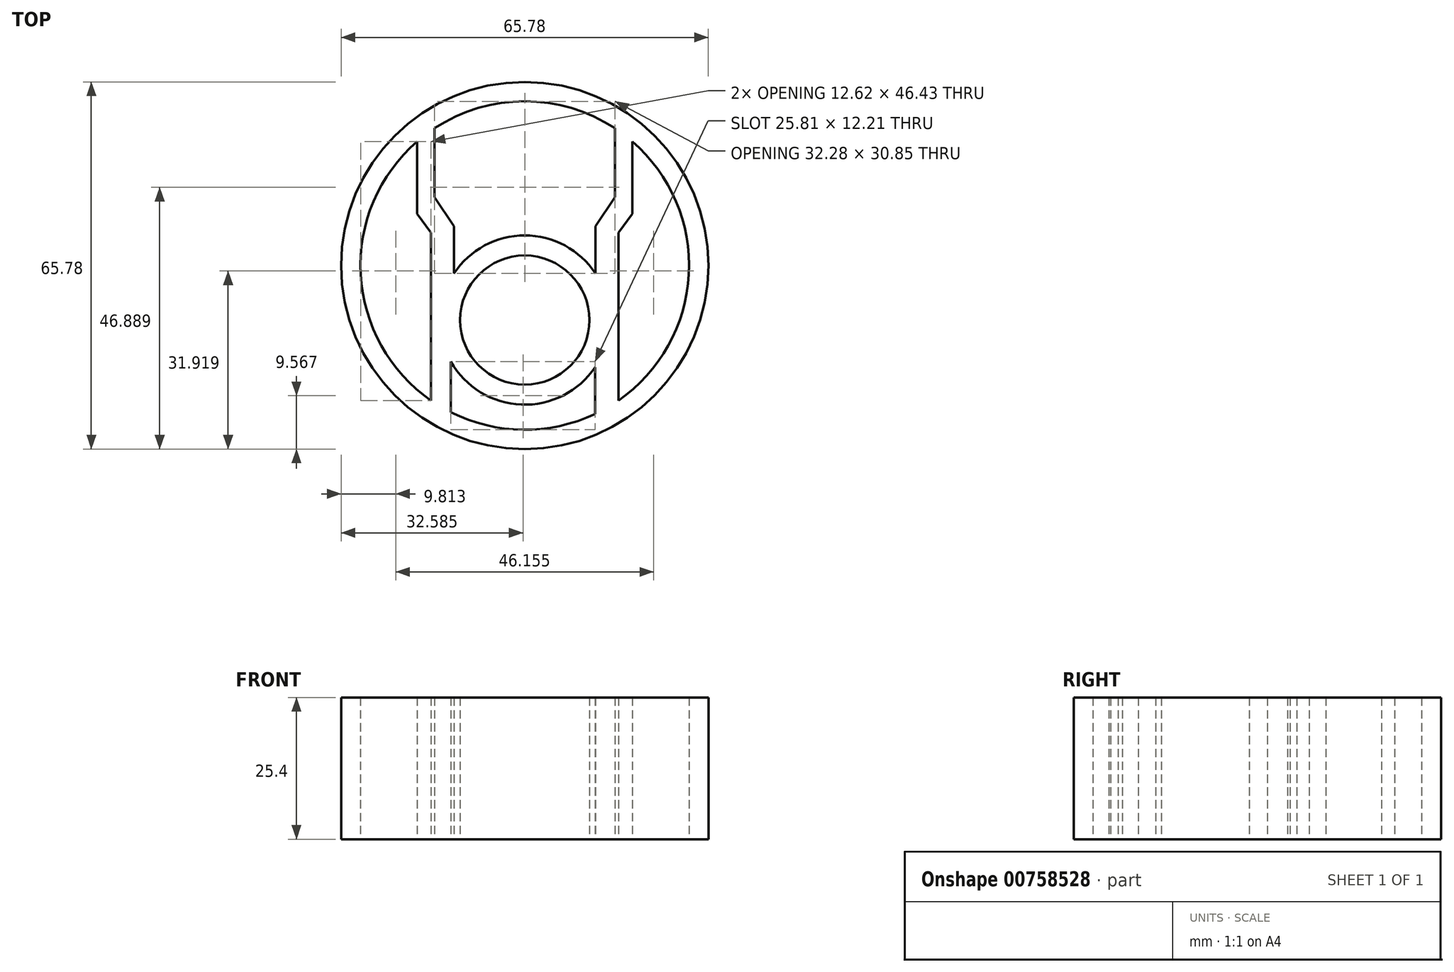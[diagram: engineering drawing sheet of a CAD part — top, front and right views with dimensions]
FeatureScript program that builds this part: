
annotation { "Feature Type Name" : "Feature", "Feature Type Description" : "" }
export const myFeature = defineFeature(function(context is Context, id is Id, definition is map)
    precondition{}
    {
        {
            var Q0;
            Q0=qCreatedBy(makeId("Top.planeOp"),FACE);
            var sketch = newSketch(context, id + "F0", { "sketchPlane" : qUnion([Q0])});
            skCircle(sketch, "E0", {"center": v(36.28, 37) * mm, "radius": 32.9 * mm});
            skArc(sketch, "E1", {"start": v(23.07, 10.7) * mm, "mid": v(35.94, 7.57) * mm, "end": v(48.88, 10.4) * mm});
            skCircle(sketch, "E2", {"center": v(36.28, 27.23) * mm, "radius": 11.58 * mm});
            skArc(sketch, "E3", {"start": v(23.07, 19.78) * mm, "mid": v(35.7, 12.07) * mm, "end": v(48.88, 18.79) * mm});
            skLineSegment(sketch, "E4", {"start": v(48.88, 10.4) * mm, "end": v(48.88, 18.79) * mm});
            skLineSegment(sketch, "E5", {"start": v(23.07, 10.7) * mm, "end": v(23.07, 19.78) * mm});
            skLineSegment(sketch, "E6", {"start": v(19.51, 12.81) * mm, "end": v(19.51, 42.89) * mm});
            skLineSegment(sketch, "E7", {"start": v(19.51, 42.89) * mm, "end": v(17.02, 46.27) * mm});
            skLineSegment(sketch, "E8", {"start": v(17.02, 46.27) * mm, "end": v(17.02, 59.24) * mm});
            skLineSegment(sketch, "E9", {"start": v(20.14, 61.6) * mm, "end": v(20.14, 49.28) * mm});
            skLineSegment(sketch, "E10", {"start": v(20.14, 49.28) * mm, "end": v(23.62, 44.05) * mm});
            skLineSegment(sketch, "E11", {"start": v(23.62, 44.05) * mm, "end": v(23.62, 35.57) * mm});
            skLineSegment(sketch, "E12.MirrorCS", {"start": v(55.54, 46.27) * mm, "end": v(55.54, 59.24) * mm});
            skLineSegment(sketch, "E13.MirrorCS", {"start": v(53.05, 42.89) * mm, "end": v(55.54, 46.27) * mm});
            skLineSegment(sketch, "E14.MirrorCS", {"start": v(53.05, 12.81) * mm, "end": v(53.05, 42.89) * mm});
            skLineSegment(sketch, "E15.MirrorCS", {"start": v(48.95, 44.05) * mm, "end": v(48.95, 35.57) * mm});
            skLineSegment(sketch, "E16.MirrorCS", {"start": v(52.42, 49.28) * mm, "end": v(48.95, 44.05) * mm});
            skLineSegment(sketch, "E17.MirrorCS", {"start": v(52.42, 61.6) * mm, "end": v(52.42, 49.28) * mm});
            skArc(sketch, "E18.trimOffspring", {"start": v(48.95, 35.57) * mm, "mid": v(36.28, 42.4) * mm, "end": v(23.62, 35.57) * mm});
            skArc(sketch, "E19.trimOffspring", {"start": v(53.05, 12.81) * mm, "mid": v(65.67, 35.42) * mm, "end": v(55.54, 59.24) * mm});
            skArc(sketch, "E20.trimOffspring", {"start": v(17.02, 59.24) * mm, "mid": v(6.9, 35.42) * mm, "end": v(19.51, 12.81) * mm});
            skArc(sketch, "E21.trimOffspring", {"start": v(52.42, 61.6) * mm, "mid": v(36.28, 66.43) * mm, "end": v(20.14, 61.6) * mm});
            skSolve(sketch);
        }
        {
            var Q0;
            Q0=makeQuery(id+"F0.imprint","IMPRINT",FACE,{"disambiguationData":[TD([[makeQuery(id+"F0.imprint","IMPRINT",EDGE,{"derivedFrom":sQuery(id+"F0.wireOp",EDGE,"E0")}),1.0]])]});
            extrude(context, id + "F1", {"entities" : qUnion([Q0]), "depth" : 25.4 * mm, "offsetDistance" : 25.4 * mm});
        }
    });
